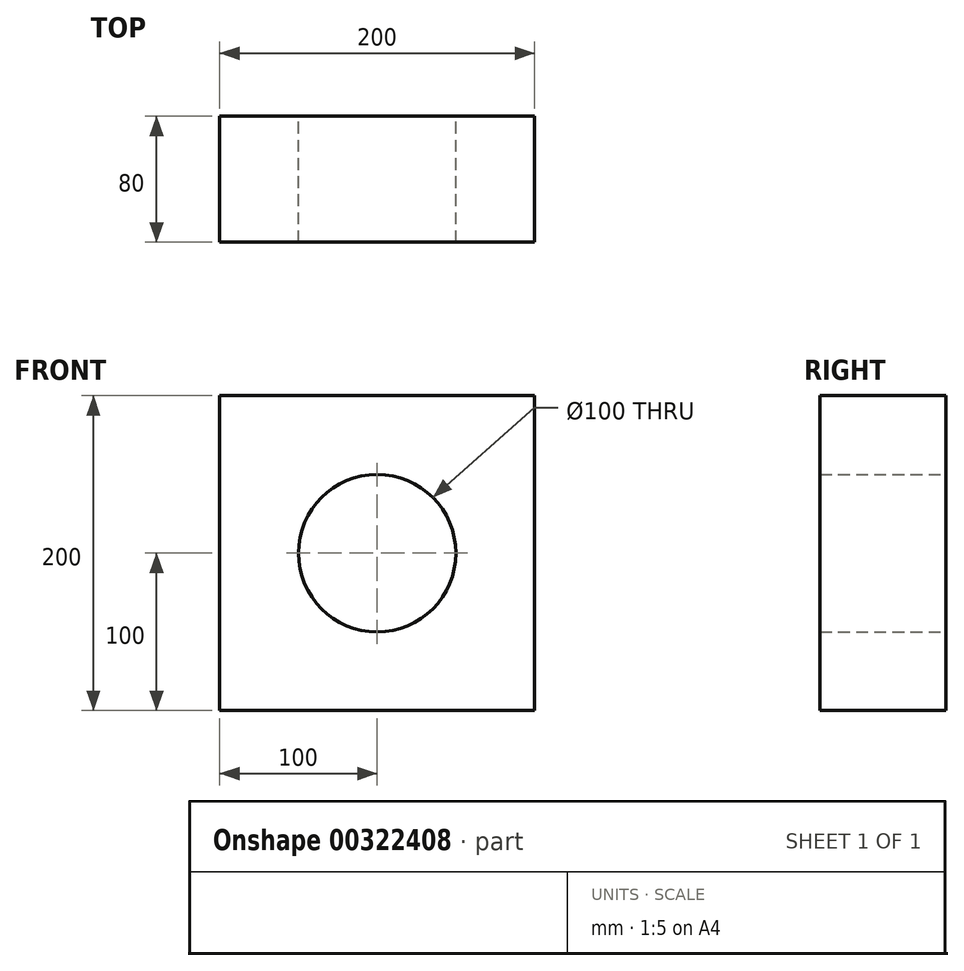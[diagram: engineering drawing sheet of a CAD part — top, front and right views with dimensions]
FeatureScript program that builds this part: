
annotation { "Feature Type Name" : "Feature", "Feature Type Description" : "" }
export const myFeature = defineFeature(function(context is Context, id is Id, definition is map)
    precondition{}
    {
        {
            var Q0;
            Q0=qCreatedBy(makeId("Front.planeOp"),FACE);
            var sketch = newSketch(context, id + "F0", { "sketchPlane" : qUnion([Q0])});
            skLineSegment(sketch, "E0.bottom", {"start": v(100, 100) * mm, "end": v(-100, 100) * mm});
            skLineSegment(sketch, "E0.top", {"start": v(100, -100) * mm, "end": v(-100, -100) * mm});
            skLineSegment(sketch, "E0.left", {"start": v(100, 100) * mm, "end": v(100, -100) * mm});
            skLineSegment(sketch, "E0.right", {"start": v(-100, 100) * mm, "end": v(-100, -100) * mm});
            skPoint(sketch, "E0.middle", {"position": v(0, 0) * mm});
            skCircle(sketch, "E1", {"center": v(0, 0) * mm, "radius": 50 * mm});
            skSolve(sketch);
        }
        {
            var Q0;
            Q0=makeQuery(id+"F0.imprint","IMPRINT",FACE,{"disambiguationData":[TD([[makeQuery(id+"F0.imprint","IMPRINT",EDGE,{"derivedFrom":sQuery(id+"F0.wireOp",EDGE,"E0.bottom")}),1.0]])]});
            extrude(context, id + "F1", {"entities" : qUnion([Q0]), "depth" : 80 * mm});
        }
    });
